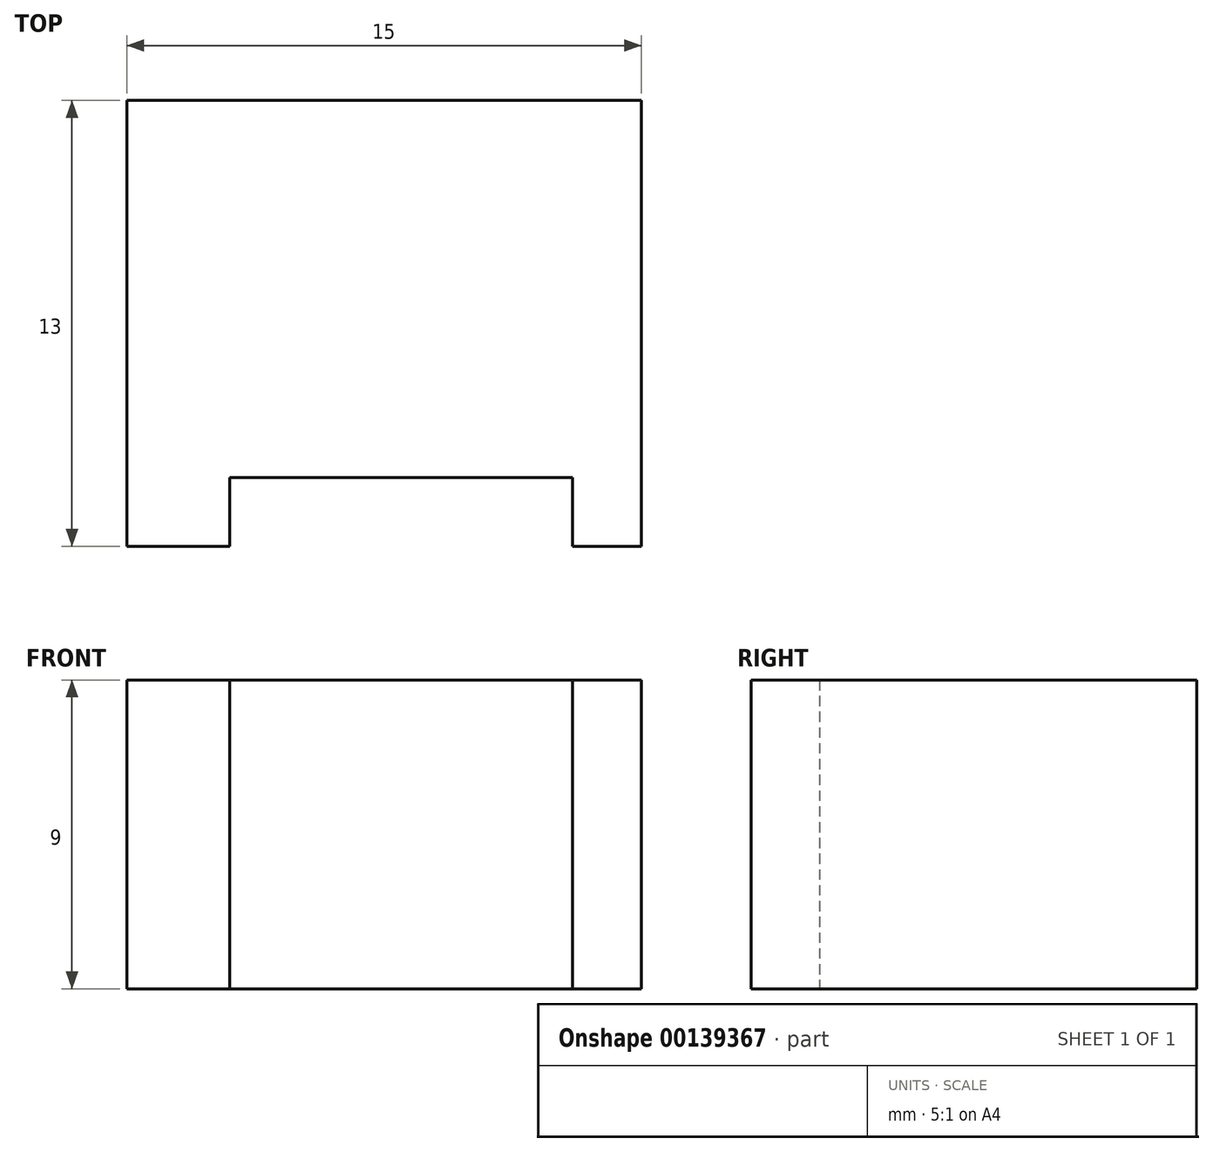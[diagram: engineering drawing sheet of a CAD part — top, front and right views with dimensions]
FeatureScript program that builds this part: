
annotation { "Feature Type Name" : "Feature", "Feature Type Description" : "" }
export const myFeature = defineFeature(function(context is Context, id is Id, definition is map)
    precondition{}
    {
        {
            var Q0;
            Q0=qCreatedBy(makeId("Top.planeOp"),FACE);
            var sketch = newSketch(context, id + "F0", { "sketchPlane" : qUnion([Q0])});
            skLineSegment(sketch, "E0.bottom", {"start": v(-7.5, 6.5) * mm, "end": v(7.5, 6.5) * mm});
            skLineSegment(sketch, "E0.top", {"start": v(-7.5, -6.5) * mm, "end": v(7.5, -6.5) * mm});
            skLineSegment(sketch, "E0.left", {"start": v(-7.5, 6.5) * mm, "end": v(-7.5, -6.5) * mm});
            skLineSegment(sketch, "E0.right", {"start": v(7.5, 6.5) * mm, "end": v(7.5, -6.5) * mm});
            skPoint(sketch, "E0.middle", {"position": v(0, 0) * mm});
            skLineSegment(sketch, "E1.bottom", {"start": v(-4.5, -6.5) * mm, "end": v(5.5, -6.5) * mm});
            skLineSegment(sketch, "E1.top", {"start": v(-4.5, -4.5) * mm, "end": v(5.5, -4.5) * mm});
            skLineSegment(sketch, "E1.left", {"start": v(-4.5, -6.5) * mm, "end": v(-4.5, -4.5) * mm});
            skLineSegment(sketch, "E1.right", {"start": v(5.5, -6.5) * mm, "end": v(5.5, -4.5) * mm});
            skSolve(sketch);
        }
        {
            var Q0;
            Q0=makeQuery(id+"F0.imprint","IMPRINT",FACE,{"disambiguationData":[TD([[makeQuery(id+"F0.imprint","IMPRINT",EDGE,{"derivedFrom":sQuery(id+"F0.wireOp",EDGE,"E0.bottom")}),-1.0]])]});
            extrude(context, id + "F1", {"entities" : qUnion([Q0]), "depth" : 9 * mm});
        }
    });
